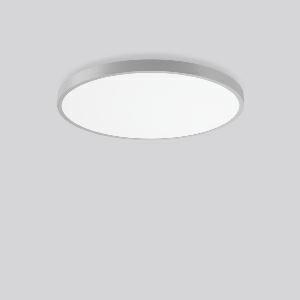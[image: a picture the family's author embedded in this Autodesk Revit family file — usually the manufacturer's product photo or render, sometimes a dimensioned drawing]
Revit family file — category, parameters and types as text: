
# Revit family: triona_round_a_312388_004_76_7f14
name_source: partatom
category: Lighting Fixtures
units: mm (PartAtom-declared; Revit-internal decimal feet)

## family parameters
Cut with Voids When Loaded = No
Host = Face
Light Source = No
Part Type = Normal
Room Calculation Point = No
Round Connector Dimension = Use Diameter
Shared = No

## types (1)
- TRIONA round A (1 x LED Modul 830, 12400 lm, 3000)
    Apparent Load = 133 VA
    CIE Flux Codes = 49 80 96 71 100
    Color Rendering = 80
    Color Temperature = 3000
    Default Elevation = 1800 mm
    Description = Series: TRIONA round
Decorative round LED surface-mounted luminaire. Flat, seamless frame: aluminium extrusion profile, powder coated. Cover made of sheet steel, powder-coated. Direct light emission through a diffuser plastic opal. Indirect light emission through a flush diffuser made of satin-finish plastic. Lightguide and diffuser made of non-yellowing plastic (PMMA). Lateral light emission (RZB SIDELITE technology) for above-average homogeneous light distribution. Direct 70%, indirect 30% light emission. Suitable for Ceiling mounting, Wall (surface). Tool-free mounting via bayonet connection. Electronic ballast included. Very easy installation thanks to Plug+Play connection. 
Colour: silver, matt (approx. RAL 9006)
Diameter: 845 mm
Height: 88 mm
Lamp: LED
Socket: without socket
Colour temperature: 3000K
Colour rendering index (CRI): 80
System power: 133 W
Rated luminous flux: 12400 lm
Luminous efficiency: 93 lm/W
Control gear: Converter, dimmable, DALI
Protection class: I
Type of protection: IP 20
    Height = 88 mm
    Lamp = 1 x LED Modul 830
    Lamp Light Flux = 12400 lm
    Lamp count = 1
    Length = 845 mm
    Lifetime = 50000 h
    Luminous efficacy = 93 lm/W
    Manufacturer = RZB
    ModVariant = No
    Model = 312388.004.76
    Mounting Place = Ceiling
    Mounting Type = Surface mounted
    Number of Poles = 1
    OnlyDefault = Yes
    Power Factor = 1
    Product Name = TRIONA round A
    Product group = Surface mounted modular luminaires
    ProductGroupID = 306
    Protection Class = Protection class I
    Protection Degree = IP 20
    RLX_Detail_Level = 1
    RLX_Emergency_Light_Flux = 0 lm
    RLX_Emergency_Type = 0
    RLX_Emergency_Type_DB = No
    RlxData = <blob elided: 41157 chars, md5=ab66b272>
    Socket = socket
    Standby Power = 0 W
    System Light Flux = 12400 lm
    System Power = 133 W
    Type Comments = Product without accessories
    Type Image = 312388.004.jpg
    URL = http://relux.com
    VarID = ---
    Voltage = 230 V
    Voltage Range = 220-240 V
    Weight = 0.00 kg
    Width = 0 mm  [stored 0 ft]

note: [stored X ft] marks values corroborated as IEEE doubles in the binary element streams (Revit-internal decimal feet)

## geometry (parser evidence)
native form markers: Blend x4, Sweep x12
no freeform markers — native parametric forms only
